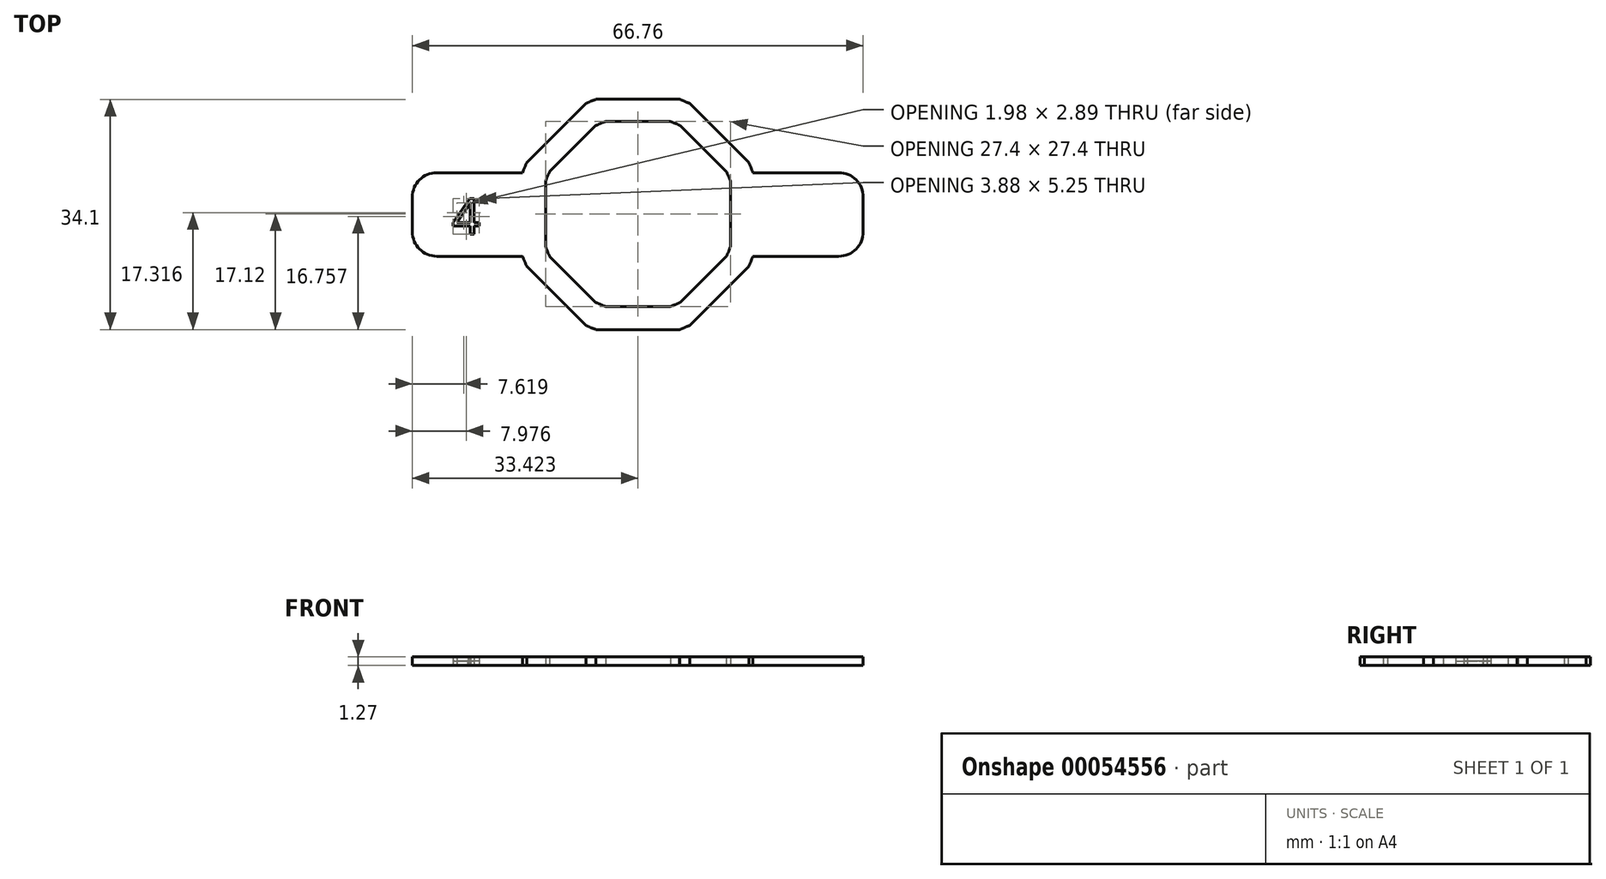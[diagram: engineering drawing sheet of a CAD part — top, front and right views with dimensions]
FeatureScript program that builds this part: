
annotation { "Feature Type Name" : "Feature", "Feature Type Description" : "" }
export const myFeature = defineFeature(function(context is Context, id is Id, definition is map)
    precondition{}
    {
        {
            var Q0;
            Q0=qCreatedBy(makeId("Top.planeOp"),FACE);
            var sketch = newSketch(context, id + "F0", { "sketchPlane" : qUnion([Q0])});
            skArc(sketch, "E0", {"start": v(-16.44, 7.68) * mm, "mid": v(-16.76, 6.94) * mm, "end": v(-17.05, 6.19) * mm});
            skLineSegment(sketch, "E1", {"start": v(-6.19, 17.05) * mm, "end": v(6.19, 17.05) * mm});
            skPoint(sketch, "E2.end.orphan", {"position": v(0, 17.05) * mm});
            skPoint(sketch, "E2.start.orphan", {"position": v(0, 18.14) * mm});
            skLineSegment(sketch, "E3.1.0", {"start": v(-16.44, 7.68) * mm, "end": v(-7.68, 16.44) * mm});
            skLineSegment(sketch, "E3.2.0", {"start": v(-17.05, -6.19) * mm, "end": v(-17.05, 6.19) * mm});
            skLineSegment(sketch, "E3.3.0", {"start": v(-7.68, -16.44) * mm, "end": v(-16.44, -7.68) * mm});
            skLineSegment(sketch, "E3.4.0", {"start": v(6.19, -17.05) * mm, "end": v(-6.19, -17.05) * mm});
            skLineSegment(sketch, "E3.5.0", {"start": v(16.44, -7.68) * mm, "end": v(7.68, -16.44) * mm});
            skLineSegment(sketch, "E3.6.0", {"start": v(17.05, 6.19) * mm, "end": v(17.05, -6.19) * mm});
            skLineSegment(sketch, "E3.7.0", {"start": v(7.68, 16.44) * mm, "end": v(16.44, 7.68) * mm});
            skArc(sketch, "E4.trimOffspring", {"start": v(-6.19, 17.05) * mm, "mid": v(-6.94, 16.76) * mm, "end": v(-7.68, 16.44) * mm});
            skArc(sketch, "E5.trimOffspring", {"start": v(7.68, 16.44) * mm, "mid": v(6.94, 16.76) * mm, "end": v(6.19, 17.05) * mm});
            skArc(sketch, "E6.trimOffspring", {"start": v(17.05, 6.19) * mm, "mid": v(16.76, 6.94) * mm, "end": v(16.44, 7.68) * mm});
            skArc(sketch, "E7.trimOffspring", {"start": v(16.44, -7.68) * mm, "mid": v(16.76, -6.94) * mm, "end": v(17.05, -6.19) * mm});
            skArc(sketch, "E8.trimOffspring", {"start": v(-7.68, -16.44) * mm, "mid": v(-6.94, -16.76) * mm, "end": v(-6.19, -17.05) * mm});
            skArc(sketch, "E9.trimOffspring", {"start": v(-17.05, -6.19) * mm, "mid": v(-16.76, -6.94) * mm, "end": v(-16.44, -7.68) * mm});
            skArc(sketch, "E10.trimOffspring", {"start": v(6.19, -17.05) * mm, "mid": v(6.94, -16.76) * mm, "end": v(7.68, -16.44) * mm});
            skLineSegment(sketch, "E11.6.0", {"start": v(13.74, 4.87) * mm, "end": v(13.74, -4.73) * mm});
            skLineSegment(sketch, "E11.4.0", {"start": v(4.84, -13.63) * mm, "end": v(-4.76, -13.63) * mm});
            skLineSegment(sketch, "E11.3.0", {"start": v(-6.25, -13) * mm, "end": v(-13.04, -6.22) * mm});
            skLineSegment(sketch, "E11.7.0", {"start": v(6.34, 13.15) * mm, "end": v(13.12, 6.36) * mm});
            skLineSegment(sketch, "E11.5.0", {"start": v(13.12, -6.22) * mm, "end": v(6.34, -13) * mm});
            skPoint(sketch, "E12.start.orphan", {"position": v(0.04, 14.58) * mm});
            skLineSegment(sketch, "E11.2.0", {"start": v(-13.65, -4.73) * mm, "end": v(-13.65, 4.87) * mm});
            skLineSegment(sketch, "E11.1.0", {"start": v(-13.04, 6.36) * mm, "end": v(-6.25, 13.15) * mm});
            skLineSegment(sketch, "E13", {"start": v(-4.76, 13.77) * mm, "end": v(4.84, 13.77) * mm});
            skPoint(sketch, "E12.end.orphan", {"position": v(0.04, 13.77) * mm});
            skPoint(sketch, "E11.center", {"position": v(0.04, 0.07) * mm});
            skArc(sketch, "E14.trimOffspring", {"start": v(4.84, -13.63) * mm, "mid": v(5.6, -13.34) * mm, "end": v(6.34, -13) * mm});
            skArc(sketch, "E15.trimOffspring", {"start": v(6.34, 13.15) * mm, "mid": v(5.6, 13.48) * mm, "end": v(4.84, 13.77) * mm});
            skArc(sketch, "E16.trimOffspring", {"start": v(-4.76, 13.77) * mm, "mid": v(-5.51, 13.48) * mm, "end": v(-6.25, 13.15) * mm});
            skArc(sketch, "E17", {"start": v(-13.04, 6.36) * mm, "mid": v(-13.37, 5.62) * mm, "end": v(-13.65, 4.87) * mm});
            skArc(sketch, "E18.trimOffspring", {"start": v(13.74, 4.87) * mm, "mid": v(13.45, 5.62) * mm, "end": v(13.12, 6.36) * mm});
            skArc(sketch, "E19.trimOffspring", {"start": v(-13.65, -4.73) * mm, "mid": v(-13.37, -5.48) * mm, "end": v(-13.04, -6.22) * mm});
            skArc(sketch, "E20.trimOffspring", {"start": v(-6.25, -13) * mm, "mid": v(-5.51, -13.34) * mm, "end": v(-4.76, -13.63) * mm});
            skArc(sketch, "E21.trimOffspring", {"start": v(13.12, -6.22) * mm, "mid": v(13.45, -5.48) * mm, "end": v(13.74, -4.73) * mm});
            skLineSegment(sketch, "E22.bottom", {"start": v(-17.05, 6.19) * mm, "end": v(-29.75, 6.19) * mm});
            skLineSegment(sketch, "E22.top", {"start": v(-17.05, -6.19) * mm, "end": v(-29.75, -6.19) * mm});
            skLineSegment(sketch, "E22.right", {"start": v(-33.38, 2.56) * mm, "end": v(-33.38, -2.56) * mm});
            skLineSegment(sketch, "E23.bottom", {"start": v(17.05, 6.19) * mm, "end": v(29.75, 6.19) * mm});
            skLineSegment(sketch, "E23.top", {"start": v(17.05, -6.19) * mm, "end": v(29.75, -6.19) * mm});
            skLineSegment(sketch, "E23.right", {"start": v(33.38, 2.56) * mm, "end": v(33.38, -2.56) * mm});
            skPoint(sketch, "E24.visualSharp", {"position": v(-33.38, 6.19) * mm});
            skArc(sketch, "E24.filletArc", {"start": v(-29.75, 6.19) * mm, "mid": v(-32.32, 5.13) * mm, "end": v(-33.38, 2.56) * mm});
            skPoint(sketch, "E25.visualSharp", {"position": v(-33.38, -6.19) * mm});
            skArc(sketch, "E25.filletArc", {"start": v(-33.38, -2.56) * mm, "mid": v(-32.32, -5.13) * mm, "end": v(-29.75, -6.19) * mm});
            skPoint(sketch, "E26.visualSharp", {"position": v(33.38, 6.19) * mm});
            skArc(sketch, "E26.filletArc", {"start": v(33.38, 2.56) * mm, "mid": v(32.32, 5.13) * mm, "end": v(29.75, 6.19) * mm});
            skPoint(sketch, "E27.visualSharp", {"position": v(33.38, -6.19) * mm});
            skArc(sketch, "E27.filletArc", {"start": v(29.75, -6.19) * mm, "mid": v(32.32, -5.13) * mm, "end": v(33.38, -2.56) * mm});
            skText(sketch, "E28", { "text": "4", "fontName": "OpenSans-Regular.ttf"});
            const initialGuessF0  = {"E28": [-0.0275, -0.00292, 1, 0, 0.00527]};
            skSetInitialGuess(sketch, initialGuessF0);
            skSolve(sketch);
        }
        {
            var Q0;
            Q0=makeQuery(id+"F0.imprint","IMPRINT",FACE,{"disambiguationData":[TD([[makeQuery(id+"F0.imprint","IMPRINT",EDGE,{"derivedFrom":sQuery(id+"F0.wireOp",EDGE,"E0")}),1.0]])]});
            extrude(context, id + "F1", {"entities" : qUnion([Q0]), "depth" : 1.27 * mm});
        }
        {
            var Q0;
            Q0=makeQuery(id+"F0.imprint","IMPRINT",FACE,{"disambiguationData":[TD([[makeQuery(id+"F0.imprint","IMPRINT",EDGE,{"derivedFrom":sQuery(id+"F0.wireOp",EDGE,"E3.2.0")}),1.0]])]});
            var Q1;
            Q1=makeQuery(id+"F0.imprint","IMPRINT",FACE,{"disambiguationData":[TD([[makeQuery(id+"F0.imprint","IMPRINT",EDGE,{"derivedFrom":sQuery(id+"F0.wireOp",EDGE,"E3.6.0")}),1.0]])]});
            extrude(context, id + "F2", {"entities" : qUnion([Q0, Q1]), "operationType" : NewBodyOperationType.ADD, "depth" : 1.27 * mm});
        }
        {
            var Q0;
            Q0=makeQuery(id+"F0.imprint","IMPRINT",FACE,{"disambiguationData":[TD([[makeQuery(id+"F0.imprint","IMPRINT",EDGE,{"derivedFrom":sQuery(id+"F0.wireOp",EDGE,"E28.sketch_text.stroke-11")}),1.0]])]});
            extrude(context, id + "F3", {"entities" : qUnion([Q0]), "depth" : 1.27 * mm});
        }
        {
            var Q0;
            Q0=makeQuery(id+"F0.imprint","IMPRINT",FACE,{"disambiguationData":[TD([[makeQuery(id+"F0.imprint","IMPRINT",EDGE,{"derivedFrom":sQuery(id+"F0.wireOp",EDGE,"E28.sketch_text.stroke-0")}),-1.0]])]});
            extrude(context, id + "F4", {"entities" : qUnion([Q0]), "depth" : 0.64 * mm});
        }
    });
